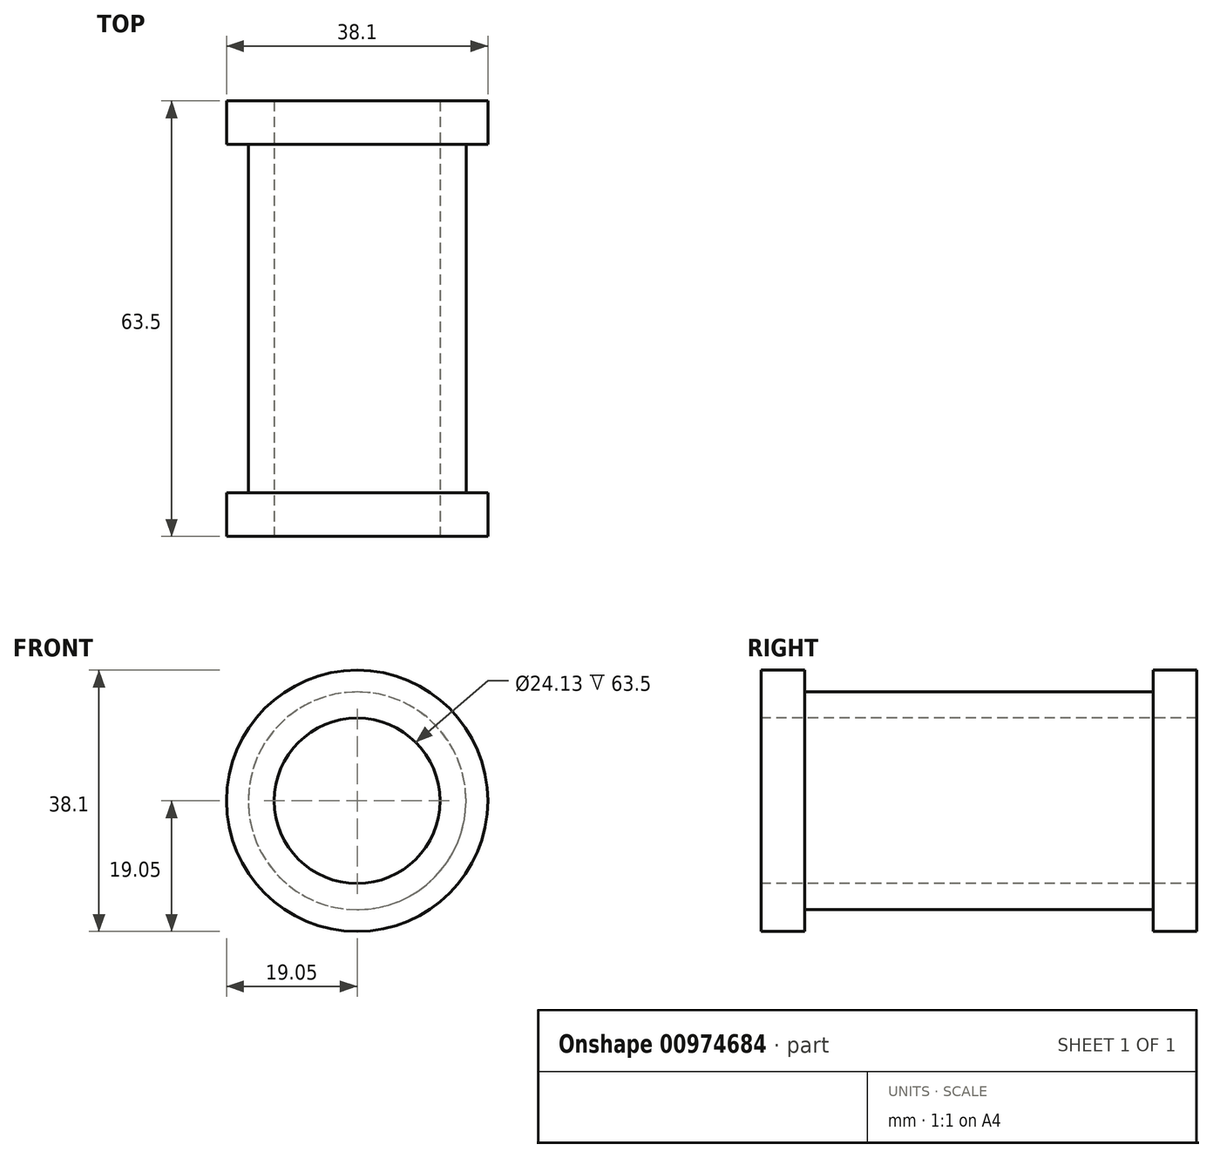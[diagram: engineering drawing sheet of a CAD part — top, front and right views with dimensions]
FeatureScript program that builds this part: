
annotation { "Feature Type Name" : "Feature", "Feature Type Description" : "" }
export const myFeature = defineFeature(function(context is Context, id is Id, definition is map)
    precondition{}
    {
        {
            var Q0;
            Q0=qCreatedBy(makeId("Front.planeOp"),FACE);
            var sketch = newSketch(context, id + "F0", { "sketchPlane" : qUnion([Q0])});
            skCircle(sketch, "E0", {"center": v(0, 0) * mm, "radius": 15.88 * mm});
            skSolve(sketch);
        }
        {
            var Q0;
            Q0=makeQuery(id+"F0.imprint","IMPRINT",FACE,{"disambiguationData":[TD([[makeQuery(id+"F0.imprint","IMPRINT",EDGE,{"derivedFrom":sQuery(id+"F0.wireOp",EDGE,"E0")}),1.0]])]});
            extrude(context, id + "F1", {"entities" : qUnion([Q0]), "endBound" : BoundingType.SYMMETRIC, "depth" : 63.5 * mm, "offsetDistance" : 25.4 * mm});
        }
        {
            var Q0;
            Q0=makeQuery(id+"F1.opExtrude","CAP_FACE",FACE,{"disambiguationData":[OSD([sQuery(id+"F0.wireOp",EDGE,"E0")])],"isStart":false});
            var sketch = newSketch(context, id + "F2", { "sketchPlane" : qUnion([Q0])});
            skCircle(sketch, "E1", {"center": v(0, 0) * mm, "radius": 19.05 * mm});
            skSolve(sketch);
        }
        {
            var Q0;
            Q0=makeQuery(id+"F2.imprint","IMPRINT",FACE,{"disambiguationData":[TD([[makeQuery(id+"F2.imprint","IMPRINT",EDGE,{"derivedFrom":sQuery(id+"F2.wireOp",EDGE,"E1")}),1.0]])]});
            extrude(context, id + "F3", {"entities" : qUnion([Q0]), "operationType" : NewBodyOperationType.ADD, "oppositeDirection" : true, "depth" : 6.35 * mm, "offsetDistance" : 25.4 * mm});
        }
        {
            var Q0;
            Q0=makeQuery(id+"F1.opExtrude","SWEPT_BODY",BODY,{"disambiguationData":[OSD([sQuery(id+"F0.wireOp",EDGE,"E0")])]});
            var Q1;
            Q1=qCreatedBy(makeId("Front.planeOp"),FACE);
            mirror(context, id + "F4", {"operationType" : NewBodyOperationType.ADD, "entities" : qUnion([Q0]), "mirrorPlane" : qUnion([Q1])});
        }
        {
            var Q0;
            {var subQ0=sQuery(id+"F0.wireOp",EDGE,"E0");Q0=makeQuery(id+"F3.boolean.opBoolean","MERGE",FACE,{"derivedFrom":[makeQuery(id+"F1.opExtrude","CAP_FACE",FACE,{"disambiguationData":[OSD([subQ0])],"isStart":false}),makeQuery(id+"F3.opExtrude","CAP_FACE",FACE,{"disambiguationData":[OSD([subQ0,sQuery(id+"F2.wireOp",EDGE,"E1")])],"isStart":true})]});}
            var sketch = newSketch(context, id + "F5", { "sketchPlane" : qUnion([Q0])});
            skCircle(sketch, "E2", {"center": v(0, 0) * mm, "radius": 12.07 * mm});
            skSolve(sketch);
        }
        {
            var Q0;
            Q0=makeQuery(id+"F5.imprint","IMPRINT",FACE,{"disambiguationData":[TD([[makeQuery(id+"F5.imprint","IMPRINT",EDGE,{"derivedFrom":sQuery(id+"F5.wireOp",EDGE,"E2")}),1.0]])]});
            extrude(context, id + "F6", {"entities" : qUnion([Q0]), "operationType" : NewBodyOperationType.REMOVE, "endBound" : BoundingType.THROUGH_ALL, "oppositeDirection" : true, "depth" : 25.4 * mm, "offsetDistance" : 25.4 * mm});
        }
    });
